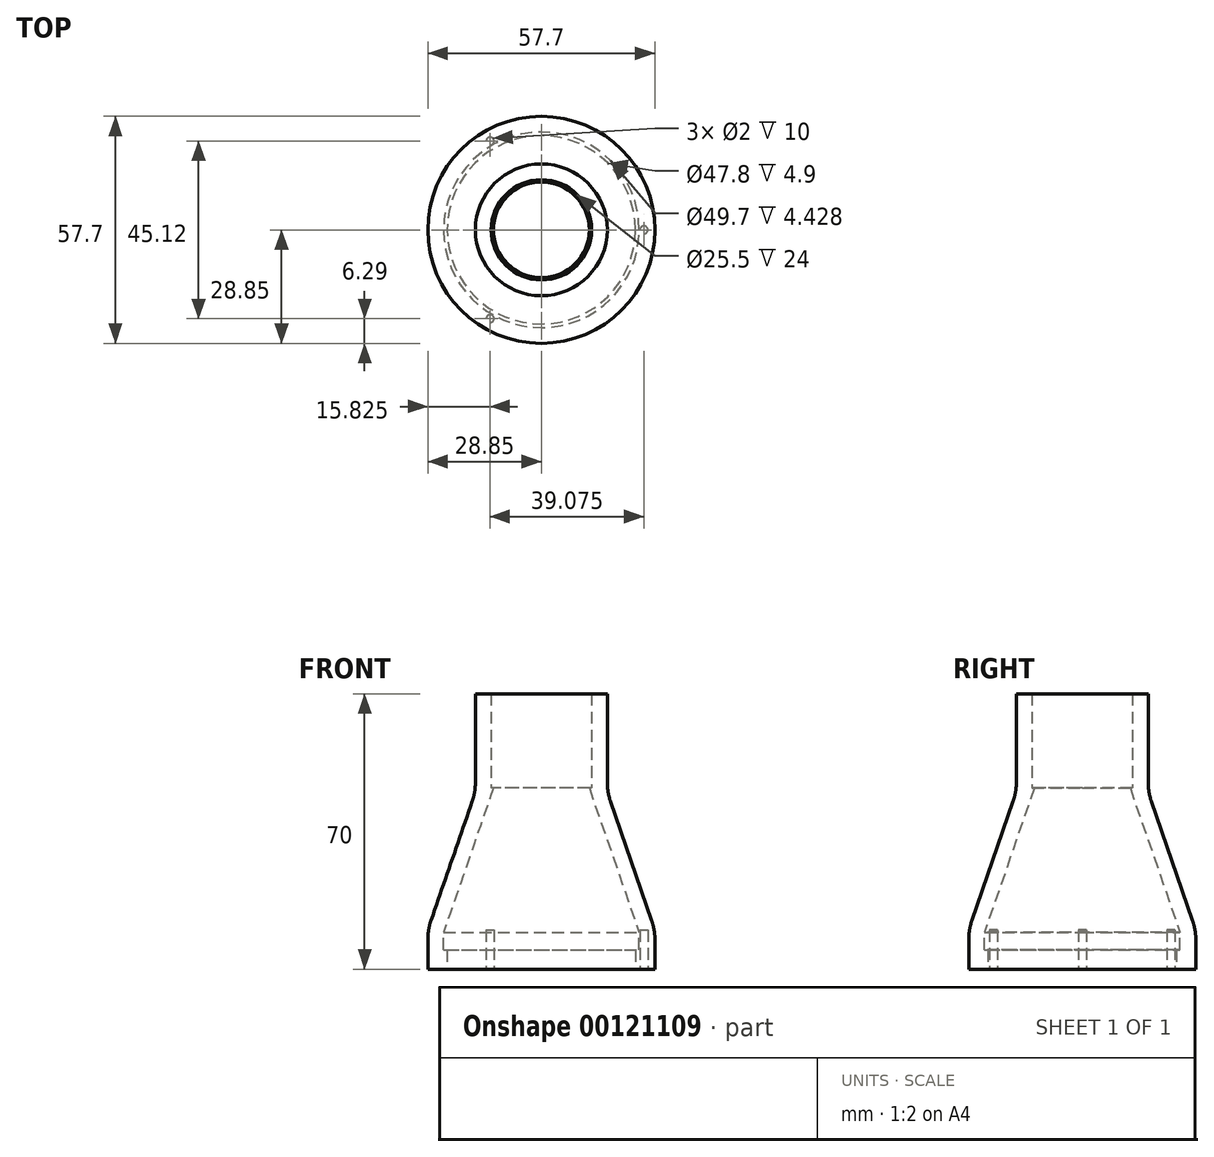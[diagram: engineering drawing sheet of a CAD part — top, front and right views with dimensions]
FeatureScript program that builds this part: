
annotation { "Feature Type Name" : "Feature", "Feature Type Description" : "" }
export const myFeature = defineFeature(function(context is Context, id is Id, definition is map)
    precondition{}
    {
        {
            var Q0;
            Q0=qCreatedBy(makeId("Top.planeOp"),FACE);
            var sketch = newSketch(context, id + "F0", { "sketchPlane" : qUnion([Q0])});
            skCircle(sketch, "E0", {"center": v(0, 0) * mm, "radius": 28.85 * mm});
            skSolve(sketch);
        }
        {
            var Q0;
            Q0=qCreatedBy(makeId("Top.planeOp"),FACE);
            cPlane(context, id + "F1", {"entities" : qUnion([Q0]), "cplaneType" : CPlaneType.OFFSET, "offset" : 35 * mm, "width" : 150 * mm, "height" : 150 * mm});
        }
        {
            var Q0;
            Q0=qCreatedBy(id+"F1.planeOp",FACE);
            var sketch = newSketch(context, id + "F2", { "sketchPlane" : qUnion([Q0])});
            skCircle(sketch, "E1", {"center": v(0, 0) * mm, "radius": 16.75 * mm});
            skSolve(sketch);
        }
        {
            var Q0;
            Q0 = qSketchRegion(id + "F2", true);
            var Q1;
            Q1 = qSketchRegion(id + "F0", true);
            loft(context, id + "F3", {"sheetProfilesArray" : [{ "sheetProfileEntities" : qUnion([Q0]) }, { "sheetProfileEntities" : qUnion([Q1]) }]});
        }
        {
            var Q0;
            Q0=makeQuery(id+"F3.opLoft","CAP_FACE",FACE,{"disambiguationData":[OSD([makeQuery(id+"F2.imprint","IMPRINT",FACE,{"disambiguationData":[TD([[makeQuery(id+"F2.imprint","IMPRINT",EDGE,{"derivedFrom":sQuery(id+"F2.wireOp",EDGE,"E1")}),1.0]])]})])],"isStart":true});
            extrude(context, id + "F4", {"entities" : qUnion([Q0]), "operationType" : NewBodyOperationType.ADD, "depth" : 25 * mm});
        }
        {
            var Q0;
            Q0=makeQuery(id+"F3.opLoft","CAP_FACE",FACE,{"disambiguationData":[OSD([makeQuery(id+"F0.imprint","IMPRINT",FACE,{"disambiguationData":[TD([[makeQuery(id+"F0.imprint","IMPRINT",EDGE,{"derivedFrom":sQuery(id+"F0.wireOp",EDGE,"E0")}),1.0]])]})])],"isStart":true});
            extrude(context, id + "F5", {"entities" : qUnion([Q0]), "operationType" : NewBodyOperationType.ADD, "depth" : 10 * mm});
        }
        {
            var Q0;
            Q0=makeQuery(id+"F5.opExtrude","CAP_FACE",FACE,{"disambiguationData":[OSD([makeQuery(id+"F0.imprint","IMPRINT",FACE,{"disambiguationData":[TD([[makeQuery(id+"F0.imprint","IMPRINT",EDGE,{"derivedFrom":sQuery(id+"F0.wireOp",EDGE,"E0")}),1.0]])]})])],"isStart":false});
            var sketch = newSketch(context, id + "F6", { "sketchPlane" : qUnion([Q0])});
            skCircle(sketch, "E2", {"center": v(0, 0) * mm, "radius": 23.9 * mm});
            skSolve(sketch);
        }
        {
            var Q0;
            Q0 = qSketchRegion(id + "F6", true);
            extrude(context, id + "F7", {"entities" : qUnion([Q0]), "operationType" : NewBodyOperationType.REMOVE, "oppositeDirection" : true, "depth" : 0.9 * mm});
        }
        {
            var Q0;
            Q0=makeQuery(id+"F4.opExtrude","CAP_FACE",FACE,{"disambiguationData":[OSD([makeQuery(id+"F2.imprint","IMPRINT",FACE,{"disambiguationData":[TD([[makeQuery(id+"F2.imprint","IMPRINT",EDGE,{"derivedFrom":sQuery(id+"F2.wireOp",EDGE,"E1")}),1.0]])]})])],"isStart":false});
            shell(context, id + "F8", {"entities" : qUnion([Q0]), "thickness" : 4 * mm});
        }
        {
            var Q0;
            Q0=makeQuery(id+"F7.boolean.opBoolean","COPY",FACE,{"derivedFrom":makeQuery(id+"F7.opExtrude","CAP_FACE",FACE,{"disambiguationData":[OSD([sQuery(id+"F6.wireOp",EDGE,"E2")])],"isStart":false})});
            var sketch = newSketch(context, id + "F9", { "sketchPlane" : qUnion([Q0])});
            skCircle(sketch, "E3.1", {"center": v(0, 0) * mm, "radius": 23.9 * mm});
            skSolve(sketch);
        }
        {
            var Q0;
            Q0 = qSketchRegion(id + "F9", true);
            extrude(context, id + "F10", {"entities" : qUnion([Q0]), "operationType" : NewBodyOperationType.REMOVE, "oppositeDirection" : true, "depth" : 5 * mm});
        }
        {
            var Q0;
            Q0=makeQuery(id+"F5.opExtrude","CAP_FACE",FACE,{"disambiguationData":[OSD([makeQuery(id+"F0.imprint","IMPRINT",FACE,{"disambiguationData":[TD([[makeQuery(id+"F0.imprint","IMPRINT",EDGE,{"derivedFrom":sQuery(id+"F0.wireOp",EDGE,"E0")}),1.0]])]})])],"isStart":false});
            var sketch = newSketch(context, id + "F11", { "sketchPlane" : qUnion([Q0])});
            skCircle(sketch, "E4", {"center": v(0, 0) * mm, "radius": 26.05 * mm, "construction": true});
            skCircle(sketch, "E5", {"center": v(26.05, 0) * mm, "radius": 1 * mm});
            skCircle(sketch, "E6.1.0", {"center": v(-13.02, 22.56) * mm, "radius": 1 * mm});
            skCircle(sketch, "E6.2.0", {"center": v(-13.03, -22.56) * mm, "radius": 1 * mm});
            skSolve(sketch);
        }
        {
            var Q0;
            Q0 = qSketchRegion(id + "F11", true);
            extrude(context, id + "F12", {"entities" : qUnion([Q0]), "operationType" : NewBodyOperationType.REMOVE, "oppositeDirection" : true, "depth" : 10 * mm});
        }
        {
            var Q0;
            {var subQ0=sQuery(id+"F2.wireOp",EDGE,"E1");Q0=makeQuery(id+"F4.boolean.opBoolean","MERGE",EDGE,{"derivedFrom":[makeQuery(id+"F3.opLoft","MID_CAP_EDGE",EDGE,{"disambiguationData":[OSD([subQ0])],"capPos":0.0}),makeQuery(id+"F4.opExtrude","CAP_EDGE",EDGE,{"disambiguationData":[OSD([subQ0])],"isStart":true})]});}
            var Q1;
            {var subQ0=sQuery(id+"F2.wireOp",EDGE,"E1");var subQ1=sQuery(id+"F0.wireOp",EDGE,"E0");Q1=makeQuery(id+"F5.boolean.opBoolean","MERGE",EDGE,{"derivedFrom":[makeQuery(id+"F3.opLoft","MID_CAP_EDGE",EDGE,{"disambiguationData":[OSD([subQ1,subQ0])],"capPos":1.0}),makeQuery(id+"F5.opExtrude","CAP_EDGE",EDGE,{"disambiguationData":[OSD([subQ1,subQ0])],"isStart":true})]});}
            fillet(context, id + "F13", {"entities" : qUnion([Q0, Q1]), "radius" : 15 * mm, "tangentPropagation" : true, "allowEdgeOverflow" : false});
        }
        {
            var Q0;
            Q0=makeQuery(id+"F4.opExtrude","CAP_FACE",FACE,{"disambiguationData":[OSD([makeQuery(id+"F2.imprint","IMPRINT",FACE,{"disambiguationData":[TD([[makeQuery(id+"F2.imprint","IMPRINT",EDGE,{"derivedFrom":sQuery(id+"F2.wireOp",EDGE,"E1")}),1.0]])]})])],"isStart":false});
            cPlane(context, id + "F14", {"entities" : qUnion([Q0]), "cplaneType" : CPlaneType.OFFSET, "offset" : 24 * mm, "oppositeDirection" : true, "width" : 150 * mm, "height" : 150 * mm});
        }
        {
            var Q0;
            Q0=qCreatedBy(id+"F14.planeOp",FACE);
            var sketch = newSketch(context, id + "F15", { "sketchPlane" : qUnion([Q0])});
            skCircle(sketch, "E7", {"center": v(0, 0) * mm, "radius": 11.95 * mm});
            skCircle(sketch, "E8.0", {"center": v(0, 0) * mm, "radius": 12.75 * mm});
            skSolve(sketch);
        }
        {
            var Q0;
            Q0 = qSketchRegion(id + "F15", true);
            var Q1;
            {var subQ0=sQuery(id+"F2.wireOp",EDGE,"E1");var subQ1=sQuery(id+"F0.wireOp",EDGE,"E0");Q1=makeQuery(id+"F8.opShell","OFFSET_FACE",FACE,{"disambiguationData":[OSD([subQ1,subQ0]),TDD([makeQuery(id+"F3.opLoft","SWEPT_FACE",FACE,{"disambiguationData":[OSD([subQ1,subQ0])]})])]});}
            extrude(context, id + "F16", {"entities" : qUnion([Q0]), "operationType" : NewBodyOperationType.ADD, "endBound" : BoundingType.UP_TO_SURFACE, "oppositeDirection" : true, "endBoundEntityFace" : qUnion([Q1]), "depth" : 3 * mm});
        }
    });
